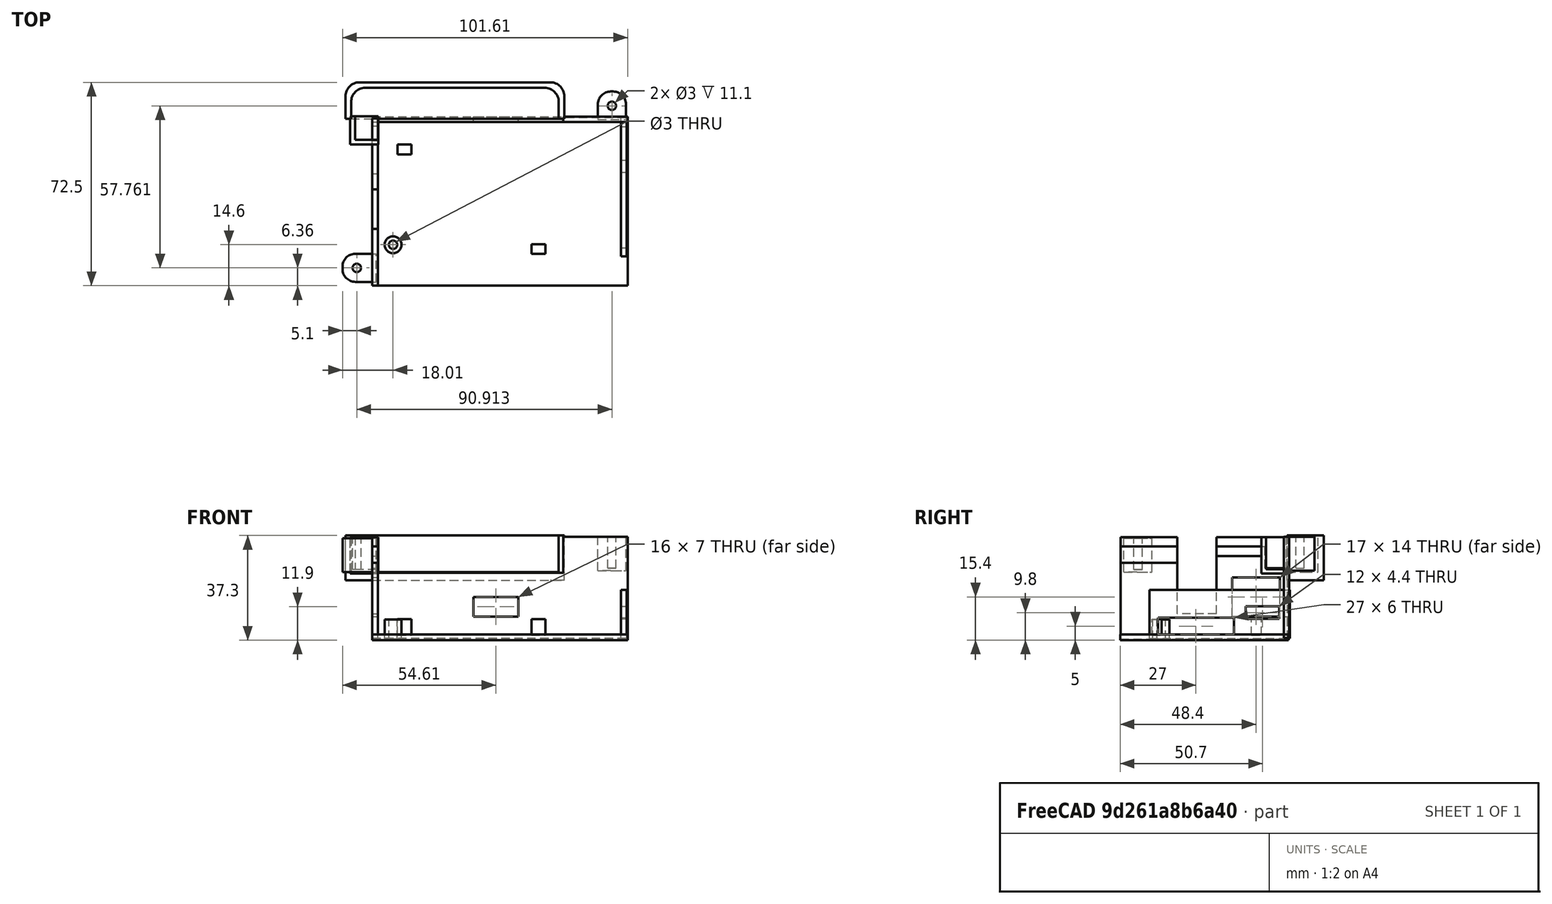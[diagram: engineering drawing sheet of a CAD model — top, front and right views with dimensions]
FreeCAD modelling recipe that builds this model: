
FCSTD DOCUMENT  (FreeCAD 0.20R29177 +426 (Git))
Label: BlipA_part1
License: All rights reserved
LicenseURL: http://en.wikipedia.org/wiki/All_rights_reserved
objects: Part::Box×21, Part::Cut×12, Part::Fillet×8, Part::Cylinder×2, Part::FeaturePython×1, Mesh::Feature×1
note: 44 computed .brp shape members not serialized (recipe doc carries the construction recipe); baked Part::Feature solids carry a one-line shape summary decoded from their .brp

FEATURE [Part::Box] Box  label="Cube"
  AttacherType = Attacher::AttachEngine3D
  Height = 16
  Length = 78
  Placement = pos=(-65,17,-13.5) rot=(0,0,1;0rad)
  Width = 13
FEATURE [Part::Fillet] Fillet
  Base = -> Box
  Edges = 1 edges r=5: [Edge7]
FEATURE [Part::Fillet] Fillet006
  Base = -> Fillet
  Edges = 1 edges r=5: [Edge15]
FEATURE [Part::Box] Box001  label="Cube001"
  AttacherType = Attacher::AttachEngine3D
  Height = 14
  Length = 74
  Placement = pos=(-65,17,-11.5) rot=(0,0,1;0rad)
  Width = 13
FEATURE [Part::Fillet] Fillet007
  Base = -> Box001
  Edges = 1 edges r=5: [Edge7]
FEATURE [Part::Fillet] Fillet008
  Base = -> Fillet007
  Edges = 1 edges r=5: [Edge15]
  Placement = pos=(2,-2,1) rot=(0,0,1;0rad)
FEATURE [Part::Cut] Cut  label="I2C_Hosting"
  Base = -> Fillet006
  Placement = pos=(-1.54,0,4.2) rot=(0,0,1;0rad)
  Tool = -> Fillet008
FEATURE [Part::Box] Box008  label="Cube008"
  AttacherType = Attacher::AttachEngine3D
  Height = 17.3
  Length = 2
  Placement = pos=(31.6,-32,-30) rot=(0,0,1;0rad)
  Width = 50
FEATURE [Part::Box] Box009  label="PowermicroUSB"
  AttacherType = Attacher::AttachEngine3D
  Height = 4.4
  Length = 4
  Placement = pos=(30.4,2.2,-23) rot=(0,0,1;0rad)
  Width = 12
FEATURE [Part::Box] Box010  label="SDcard"
  AttacherType = Attacher::AttachEngine3D
  Height = 6
  Length = 4
  Placement = pos=(30.2,-29,-28.6) rot=(0,0,1;0rad)
  Width = 27
FEATURE [Part::Box] Box025  label="Cube025"
  AttacherType = Attacher::AttachEngine3D
  Height = 2
  Length = 91
  Placement = pos=(-57,-42.5,-30.6) rot=(0,0,1;0rad)
  Width = 60
FEATURE [Part::Box] Box029  label="Cube027"
  AttacherType = Attacher::AttachEngine3D
  Height = 36
  Length = 91
  Placement = pos=(-57,15.8,-29.8) rot=(0,0,1;0rad)
  Width = 2
FEATURE [Part::Box] Box030  label="HDMI_hole"
  AttacherType = Attacher::AttachEngine3D
  Height = 7
  Length = 16
  Placement = pos=(-21,15.5,-22.2) rot=(0,0,1;0rad)
  Width = 3
FEATURE [Part::Cut] Cut014  label="Side_HDMI"
  Base = -> Box029
  Tool = -> Box030
FEATURE [Part::Cut] Cut015
  Base = -> Box008
  Tool = -> Box009
FEATURE [Part::FeaturePython] Tube015  # WARN: FeaturePython — macro-defined, semantics opaque (R4)
  AttacherType = Attacher::AttachEngine3D
  Height = 7
  InnerRadius = 1.5
  OuterRadius = 3
  Placement = pos=(-49.6,-27.9,-30.2) rot=(0,0,1;0rad)
FEATURE [Part::Box] Box031  label="Cube028"
  AttacherType = Attacher::AttachEngine3D
  Height = 5.7
  Length = 5
  Placement = pos=(-0.3,-31.2,-28.8) rot=(0,0,1;0rad)
  Width = 3.5
FEATURE [Part::Box] Box032  label="Cube029"
  AttacherType = Attacher::AttachEngine3D
  Height = 5.7
  Length = 5
  Placement = pos=(-48,4.3,-28.8) rot=(0,0,1;0rad)
  Width = 3.5
FEATURE [Part::Box] Box033  label="Cube030"
  AttacherType = Attacher::AttachEngine3D
  Height = 12
  Length = 12
  Placement = pos=(-108.3,0,-49.2) rot=(0,0,1;0rad)
  Width = 10
FEATURE [Part::Cylinder] Cylinder002  label="Cylinder"
  Angle = 360
  AttacherType = Attacher::AttachEngine3D
  FirstAngle = 0
  Height = 20
  Placement = pos=(-103.2,5,-48.3) rot=(0,0,1;0rad)
  Radius = 1.5
  SecondAngle = 0
FEATURE [Part::Cut] Cut017
  Base = -> Box033
  Tool = -> Cylinder002
FEATURE [Part::Fillet] Fillet011
  Base = -> Cut017
  Edges = 1 edges r=4.5: [Edge3]
FEATURE [Part::Fillet] Fillet012
  Base = -> Fillet011
  Edges = 1 edges r=4.6: [Edge2]
  Placement = pos=(40.69,-41.14,42.87) rot=(0,0,1;0rad)
FEATURE [Part::Box] Box034  label="Cube031"
  AttacherType = Attacher::AttachEngine3D
  Height = 16
  Length = 68
  Placement = pos=(-57,9,-6.62) rot=(0,0,1;0rad)
  Width = 10
FEATURE [Part::Cut] Cut018
  Base = -> Cut014
  Tool = -> Box034
FEATURE [Part::Cut] Cut016  label="side_PowerSDCard"
  Base = -> Cut015
  Tool = -> Box010
FEATURE [Part::Box] Box037  label="Cube034"
  AttacherType = Attacher::AttachEngine3D
  Height = 12
  Length = 10
  Placement = pos=(-108.3,0,-49.2) rot=(0,0,1;0rad)
  Width = 10
FEATURE [Part::Cylinder] Cylinder003
  Angle = 360
  AttacherType = Attacher::AttachEngine3D
  FirstAngle = 0
  Height = 20
  Placement = pos=(-103.2,5,-48.3) rot=(0,0,1;0rad)
  Radius = 1.5
  SecondAngle = 0
FEATURE [Part::Cut] Cut020
  Base = -> Box037
  Tool = -> Cylinder003
FEATURE [Part::Fillet] Fillet013
  Base = -> Cut020
  Edges = 1 edges r=4.5: [Edge3]
FEATURE [Part::Fillet] Fillet014
  Base = -> Fillet013
  Edges = 1 edges r=4.6: [Edge2]
  Placement = pos=(23.403,-81.5794,43.36) rot=(0,0,-1;1.5708rad)
FEATURE [Part::Box] Box045  label="Cubo"
  AttacherType = Attacher::AttachEngine3D
  Height = 6.8
  Length = 2
  Placement = pos=(-57,-8.2,-0.7) rot=(0,0,1;0rad)
  Width = 16.2
FEATURE [Part::Box] Box046  label="Cubo001"
  AttacherType = Attacher::AttachEngine3D
  Height = 9.1
  Length = 2
  Placement = pos=(-57,-42.4,-3.02) rot=(0,0,1;0rad)
  Width = 20.2
FEATURE [Part::Box] Box047  label="Cubo002"
  AttacherType = Attacher::AttachEngine3D
  Height = 13
  Length = 10
  Placement = pos=(-64.85,7.88,-4.91) rot=(0,0,1;0rad)
  Width = 10
FEATURE [Part::Box] Box048  label="Cubo003"
  AttacherType = Attacher::AttachEngine3D
  Height = 14
  Length = 10
  Placement = pos=(-63.08,9.52,-3.39) rot=(0,0,1;0rad)
  Width = 10
FEATURE [Part::Cut] Cut028
  Base = -> Box047
  Placement = pos=(0,0,-1.95) rot=(0,0,1;0rad)
  Tool = -> Box048
FEATURE [Part::Box] Box049  label="Cubo004"
  AttacherType = Attacher::AttachEngine3D
  Height = 10
  Length = 10
  Placement = pos=(-57.27,9.14,-4.94) rot=(0,0,1;0rad)
  Width = 10
FEATURE [Part::Box] Box050  label="Ethernet001"
  AttacherType = Attacher::AttachEngine3D
  Height = 14
  Length = 4
  Placement = pos=(-58.6,-2.6,-22.2) rot=(0,0,1;0rad)
  Width = 17
FEATURE [Part::Box] Box051  label="USB001"
  AttacherType = Attacher::AttachEngine3D
  Height = 25.5
  Length = 4
  Placement = pos=(-57.6,-22.2,-21.2) rot=(0,0,1;0rad)
  Width = 14
FEATURE [Part::Box] Box052  label="Cube042"
  AttacherType = Attacher::AttachEngine3D
  Height = 33
  Length = 2
  Placement = pos=(-57,-42.4,-30.2) rot=(0,0,1;0rad)
  Width = 59.5
FEATURE [Part::Cut] Cut029
  Base = -> Box052
  Tool = -> Box051
FEATURE [Part::Cut] Cut030
  Base = -> Cut029
FEATURE [Part::Cut] Cut031
  Base = -> Cut030
  Tool = -> Box050
FEATURE [Part::Cut] Cut032
  Base = -> Cut031
  Tool = -> Box049
FEATURE [Mesh::Feature] Cover_updated  label="Cover_in_BlipA_part2"
  Placement = pos=(0,0,3.47) rot=(0,0,1;0rad)
